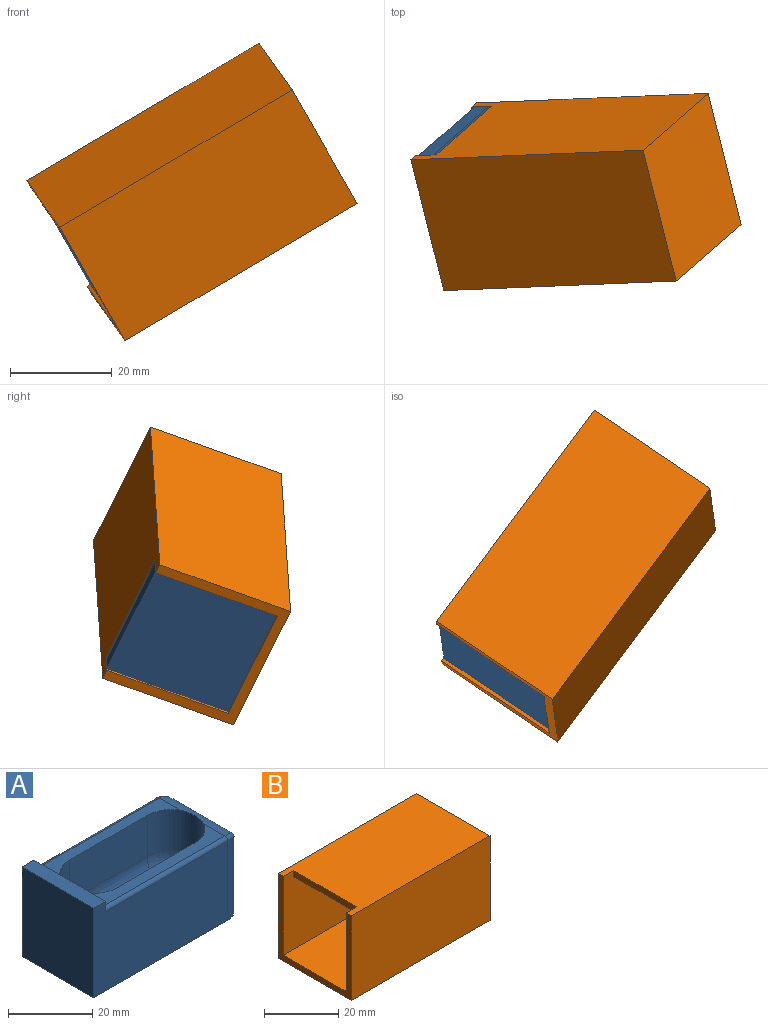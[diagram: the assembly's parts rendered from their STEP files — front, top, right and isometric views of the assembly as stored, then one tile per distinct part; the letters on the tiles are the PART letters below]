
ASSEMBLY  parts=2 mates=1
PART A: 23 faces, bbox 50x24x26 mm
  f0: plane 41x11mm, normal (0,0,1), area 145.1mm2, adj f6,f8,f9,f14,f17,f20
  f1: plane 19x14mm, normal (1,0,0), area 266mm2, adj f5,f18,f20,f22
  f2: plane 45x26mm, normal (0,1,0), area 1047mm2, adj f3,f5,f14,f15,f16,f22
  f3: plane 26x24mm, normal (-1,0,0), area 624mm2, adj f2,f4,f5,f15
  f4: plane 45x26mm, normal (0,-1,0), area 1047mm2, adj f3,f5,f14,f15,f17,f18
  f5: plane 50x24mm, normal (0,0,-1), area 1189.3mm2, adj f1,f2,f3,f4,f18,f22
  f6: cylinder r=8mm len=16mm, axis (0,0,-1), area 301.6mm2, adj f0,f7,f9,f10,f13
  f7: plane 26x12mm, normal (0,-1,0), area 312mm2, adj f6,f8,f10,f11
  f8: cylinder r=8mm len=16mm, axis (0,0,-1), area 301.2mm2, adj f0,f7,f9,f10,f12,f20
  f9: plane 26x12mm, normal (0,1,0), area 312mm2, adj f0,f6,f8,f11
  f10: plane 41x11mm, normal (0,0,1), area 145.1mm2, adj f6,f7,f8,f14,f16,f20
  f11: cylinder r=8mm len=26mm, axis (1,0,0), area 653.5mm2, adj f7,f9,f12,f13
  f12: sphere r=8mm, area 201.1mm2, adj f8,f11
  f13: sphere r=8mm, area 201.1mm2, adj f6,f11
  f14: plane 24x3mm, normal (1,0,0), area 48.4mm2, adj f0,f2,f4,f10,f15,f16,f17
  f15: plane 24x4mm, normal (0,0,1), area 96mm2, adj f2,f3,f4,f14
  f16: cylinder r=1mm len=41mm, axis (1,0,0), area 64.4mm2, adj f2,f10,f14,f21
  f17: cylinder r=1mm len=41mm, axis (-1,0,0), area 64.4mm2, adj f0,f4,f14,f19
  f18: cylinder r=5mm len=23mm, axis (0,0,-1), area 169.2mm2, adj f1,f4,f5,f19
  f19: bspline ~5.2x5mm, area 8.5mm2, adj f17,f18,f20
  f20: cylinder r=5mm len=22mm, axis (0,-1,0), area 144.7mm2, adj f0,f1,f8,f10,f19,f21
  f21: bspline ~5.2x5mm, area 8.5mm2, adj f16,f20,f22
  f22: cylinder r=5mm len=23mm, axis (0,0,1), area 169.2mm2, adj f1,f2,f5,f21
PART B: 12 faces, bbox 53x28x28 mm
  f0: plane 53x28mm, normal (0,0,1), area 1388mm2, adj f1,f2,f3,f4,f6,f8,f11
  f1: plane 28x28mm, normal (-1,0,0), area 160mm2, adj f0,f3,f4,f5,f6,f7,f8
  f2: plane 28x28mm, normal (1,0,0), area 784mm2, adj f0,f3,f4,f5
  f3: plane 53x28mm, normal (0,1,0), area 1484mm2, adj f0,f1,f2,f5
  f4: plane 53x28mm, normal (0,-1,0), area 1484mm2, adj f0,f1,f2,f5
  f5: plane 53x28mm, normal (0,0,-1), area 1484mm2, adj f1,f2,f3,f4
  f6: plane 51x26mm, normal (0,-1,0), area 1232mm2, adj f0,f1,f7,f9,f10,f11
  f7: plane 51x24mm, normal (0,0,1), area 1224mm2, adj f1,f6,f8,f10
  f8: plane 51x26mm, normal (0,1,0), area 1232mm2, adj f0,f1,f7,f9,f10,f11
  f9: plane 47x24mm, normal (0,0,-1), area 1128mm2, adj f6,f8,f10,f11
  f10: plane 24x24mm, normal (-1,0,0), area 576mm2, adj f6,f7,f8,f9
  f11: plane 24x2mm, normal (-1,0,0), area 48mm2, adj f0,f6,f8,f9
PLACE A rot(axis=(-0.9,-0.39,-0.22),73deg) t=(108.53,4.29,5.28)mm
PLACE B rot(axis=(-0.9,-0.39,-0.22),73deg) t=(109.67,2.49,5.03)mm
MATE slider A.f5 <-> B.f7  axis (0.23,-0.92,-0.33) through (108.34,4.29,5.17)mm
